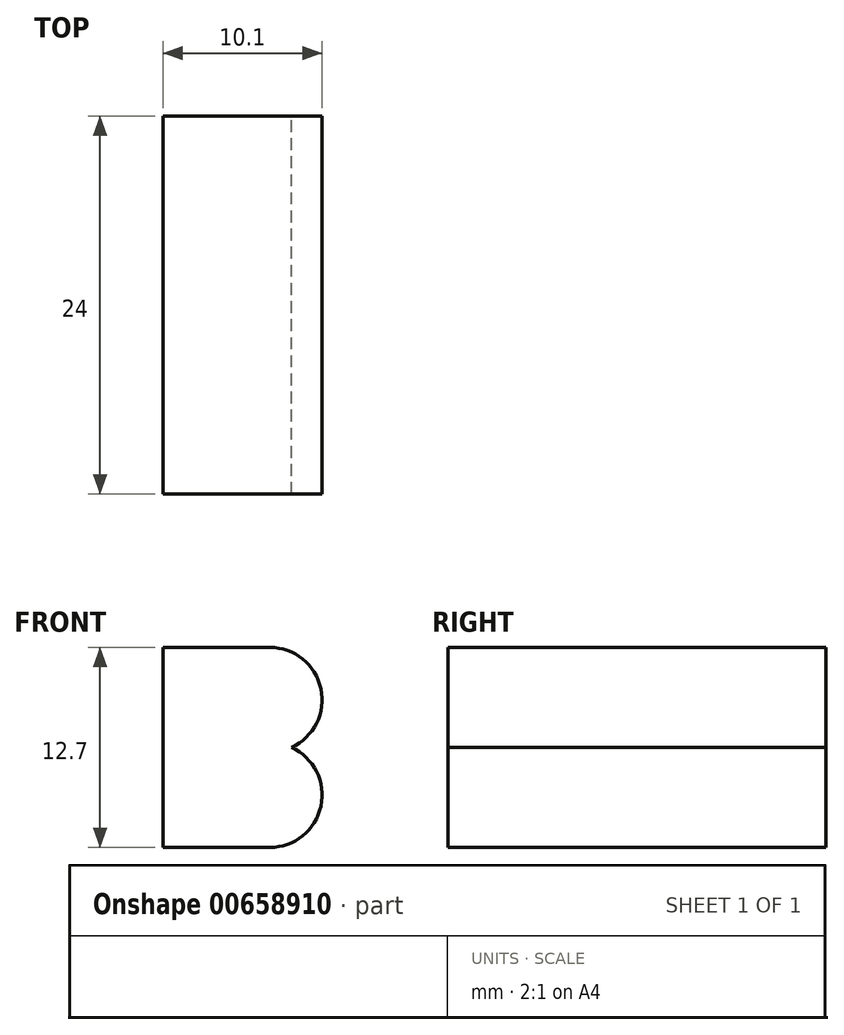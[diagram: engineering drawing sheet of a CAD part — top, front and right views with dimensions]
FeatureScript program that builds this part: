
annotation { "Feature Type Name" : "Feature", "Feature Type Description" : "" }
export const myFeature = defineFeature(function(context is Context, id is Id, definition is map)
    precondition{}
    {
        {
            var Q0;
            Q0=qCreatedBy(makeId("Front.planeOp"),FACE);
            var sketch = newSketch(context, id + "F0", { "sketchPlane" : qUnion([Q0])});
            skLineSegment(sketch, "E0.bottom", {"start": v(-5.05, 6.35) * mm, "end": v(1.73, 6.35) * mm});
            skLineSegment(sketch, "E0.top", {"start": v(-5.05, -6.35) * mm, "end": v(1.72, -6.35) * mm});
            skLineSegment(sketch, "E0.left", {"start": v(-5.05, 6.35) * mm, "end": v(-5.05, -6.35) * mm});
            skPoint(sketch, "E0.middle", {"position": v(0, 0) * mm});
            skArc(sketch, "E1", {"start": v(1.72, -6.35) * mm, "mid": v(4.97, -3.73) * mm, "end": v(3.1, 0) * mm});
            skArc(sketch, "E2", {"start": v(3.1, 0) * mm, "mid": v(4.97, 3.73) * mm, "end": v(1.73, 6.35) * mm});
            skPoint(sketch, "E3.orphan", {"position": v(5.05, 6.35) * mm});
            skPoint(sketch, "E4.orphan", {"position": v(5.05, -6.35) * mm});
            skSolve(sketch);
        }
        {
            var Q0;
            Q0=qSketchRegion(id+"F0",true);
            extrude(context, id + "F1", {"entities" : qUnion([Q0]), "depth" : 24 * mm, "offsetDistance" : 25 * mm});
        }
    });
